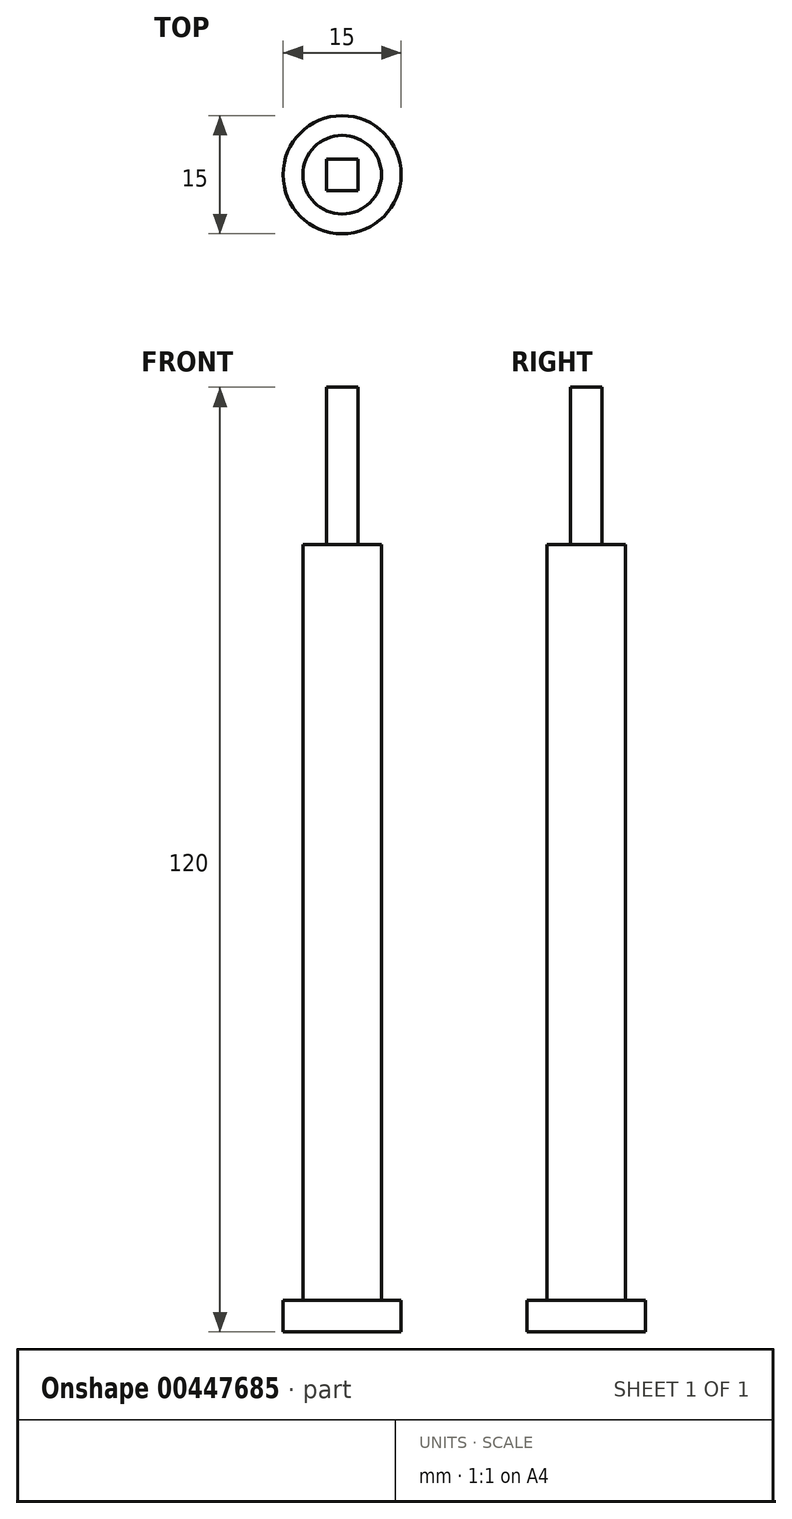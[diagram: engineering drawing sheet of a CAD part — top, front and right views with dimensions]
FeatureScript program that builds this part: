
annotation { "Feature Type Name" : "Feature", "Feature Type Description" : "" }
export const myFeature = defineFeature(function(context is Context, id is Id, definition is map)
    precondition{}
    {
        {
            var Q0;
            Q0=qCreatedBy(makeId("Top.planeOp"),FACE);
            var sketch = newSketch(context, id + "F0", { "sketchPlane" : qUnion([Q0])});
            skCircle(sketch, "E0", {"center": v(0, 0) * mm, "radius": 7.5 * mm});
            skSolve(sketch);
        }
        {
            var Q0;
            Q0 = qSketchRegion(id + "F0", true);
            extrude(context, id + "F1", {"entities" : qUnion([Q0]), "depth" : 4 * mm});
        }
        {
            var Q0;
            Q0=qCreatedBy(makeId("Top.planeOp"),FACE);
            var sketch = newSketch(context, id + "F2", { "sketchPlane" : qUnion([Q0])});
            skCircle(sketch, "E1", {"center": v(0, 0) * mm, "radius": 5 * mm});
            skSolve(sketch);
        }
        {
            var Q0;
            Q0 = qSketchRegion(id + "F2", true);
            extrude(context, id + "F3", {"entities" : qUnion([Q0]), "operationType" : NewBodyOperationType.ADD, "depth" : 100 * mm});
        }
        {
            var Q0;
            Q0=makeQuery(id+"F3.opExtrude","CAP_FACE",FACE,{"disambiguationData":[OSD([sQuery(id+"F2.wireOp",EDGE,"E1")])],"isStart":false});
            var sketch = newSketch(context, id + "F4", { "sketchPlane" : qUnion([Q0])});
            skLineSegment(sketch, "E2.bottom", {"start": v(-2, 2) * mm, "end": v(2, 2) * mm});
            skLineSegment(sketch, "E2.top", {"start": v(-2, -2) * mm, "end": v(2, -2) * mm});
            skLineSegment(sketch, "E2.left", {"start": v(-2, 2) * mm, "end": v(-2, -2) * mm});
            skLineSegment(sketch, "E2.right", {"start": v(2, 2) * mm, "end": v(2, -2) * mm});
            skSolve(sketch);
        }
        {
            var Q0;
            Q0=makeQuery(id+"F4.imprint","IMPRINT",FACE,{"disambiguationData":[TD([[makeQuery(id+"F4.imprint","IMPRINT",EDGE,{"derivedFrom":sQuery(id+"F4.wireOp",EDGE,"E2.bottom")}),-1.0]])]});
            extrude(context, id + "F5", {"entities" : qUnion([Q0]), "operationType" : NewBodyOperationType.ADD, "depth" : 20 * mm});
        }
    });
